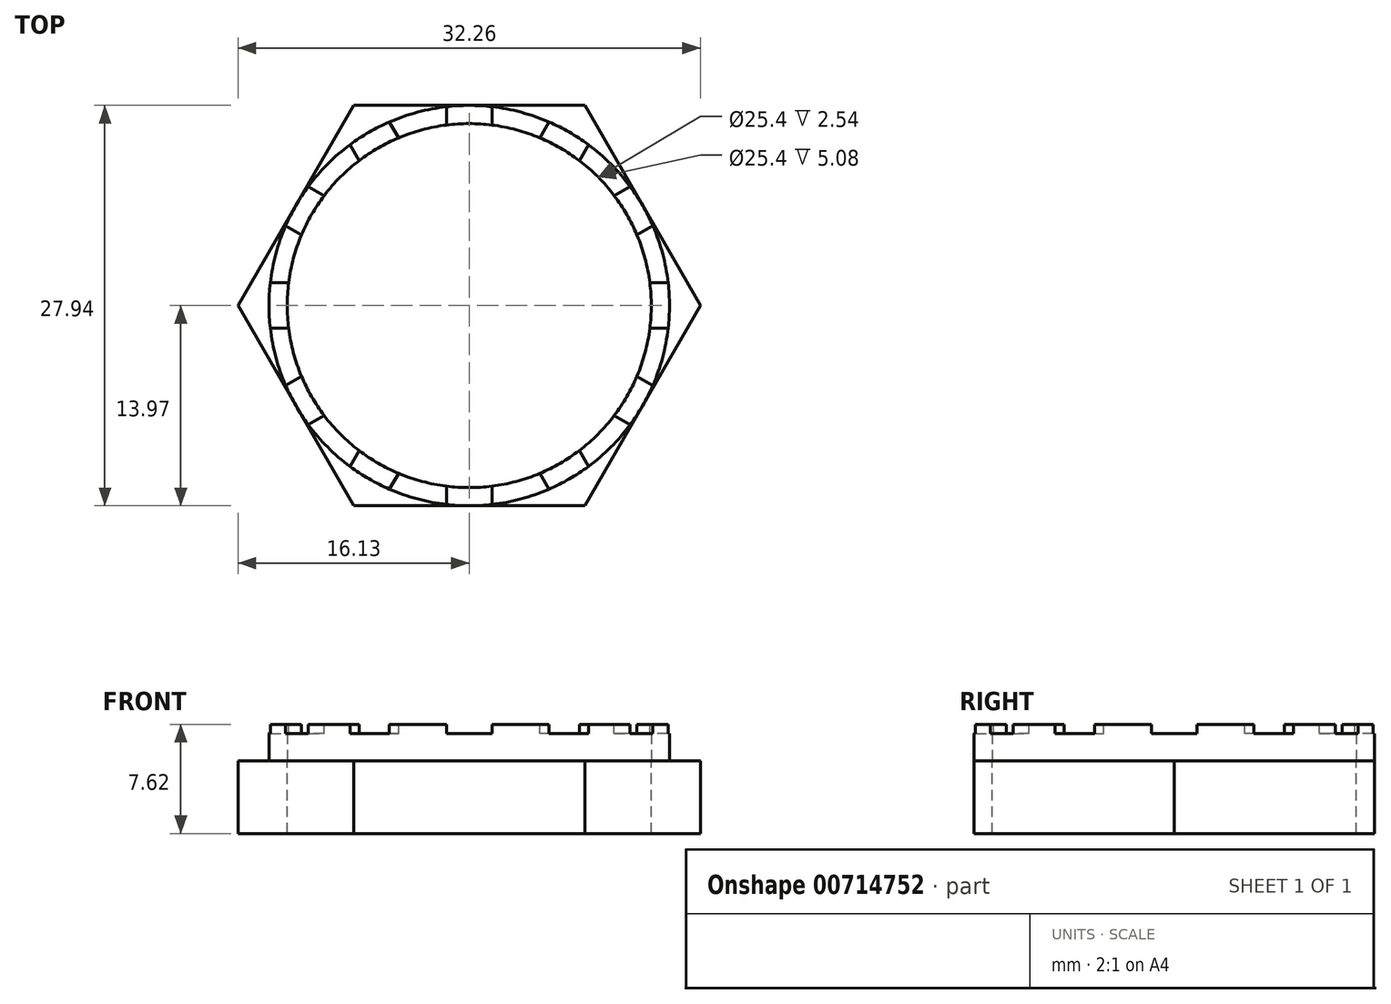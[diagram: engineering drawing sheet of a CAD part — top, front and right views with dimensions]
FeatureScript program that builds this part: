
annotation { "Feature Type Name" : "Feature", "Feature Type Description" : "" }
export const myFeature = defineFeature(function(context is Context, id is Id, definition is map)
    precondition{}
    {
        {
            var Q0;
            Q0=qCreatedBy(makeId("Top.planeOp"),FACE);
            var sketch = newSketch(context, id + "F0", { "sketchPlane" : qUnion([Q0])});
            skArc(sketch, "E0", {"start": v(1.59, 13.88) * mm, "mid": v(0, 13.97) * mm, "end": v(-1.59, 13.88) * mm});
            skArc(sketch, "E1", {"start": v(1.59, 12.6) * mm, "mid": v(0, 12.7) * mm, "end": v(-1.59, 12.6) * mm});
            skLineSegment(sketch, "E2", {"start": v(1.59, 13.88) * mm, "end": v(1.59, 12.6) * mm});
            skLineSegment(sketch, "E3", {"start": v(-1.59, 13.88) * mm, "end": v(-1.59, 12.6) * mm});
            skLineSegment(sketch, "E4.1.0", {"start": v(-8.31, 11.23) * mm, "end": v(-7.68, 10.12) * mm});
            skLineSegment(sketch, "E4.1.1", {"start": v(-5.56, 12.81) * mm, "end": v(-4.93, 11.7) * mm});
            skLineSegment(sketch, "E4.2.0", {"start": v(-12.81, 5.56) * mm, "end": v(-11.7, 4.93) * mm});
            skLineSegment(sketch, "E4.2.1", {"start": v(-11.23, 8.31) * mm, "end": v(-10.12, 7.68) * mm});
            skLineSegment(sketch, "E4.3.0", {"start": v(-13.88, -1.59) * mm, "end": v(-12.6, -1.59) * mm});
            skLineSegment(sketch, "E4.3.1", {"start": v(-13.88, 1.59) * mm, "end": v(-12.6, 1.59) * mm});
            skLineSegment(sketch, "E4.4.0", {"start": v(-11.23, -8.31) * mm, "end": v(-10.12, -7.68) * mm});
            skLineSegment(sketch, "E4.4.1", {"start": v(-12.81, -5.56) * mm, "end": v(-11.7, -4.93) * mm});
            skLineSegment(sketch, "E4.5.0", {"start": v(-5.56, -12.81) * mm, "end": v(-4.93, -11.7) * mm});
            skLineSegment(sketch, "E4.5.1", {"start": v(-8.31, -11.23) * mm, "end": v(-7.68, -10.12) * mm});
            skLineSegment(sketch, "E4.6.0", {"start": v(1.59, -13.88) * mm, "end": v(1.59, -12.6) * mm});
            skLineSegment(sketch, "E4.6.1", {"start": v(-1.59, -13.88) * mm, "end": v(-1.59, -12.6) * mm});
            skLineSegment(sketch, "E4.7.0", {"start": v(8.31, -11.23) * mm, "end": v(7.68, -10.12) * mm});
            skLineSegment(sketch, "E4.7.1", {"start": v(5.56, -12.81) * mm, "end": v(4.93, -11.7) * mm});
            skLineSegment(sketch, "E4.8.0", {"start": v(12.81, -5.56) * mm, "end": v(11.7, -4.93) * mm});
            skLineSegment(sketch, "E4.8.1", {"start": v(11.23, -8.31) * mm, "end": v(10.12, -7.68) * mm});
            skLineSegment(sketch, "E4.9.0", {"start": v(13.88, 1.59) * mm, "end": v(12.6, 1.59) * mm});
            skLineSegment(sketch, "E4.9.1", {"start": v(13.88, -1.59) * mm, "end": v(12.6, -1.59) * mm});
            skLineSegment(sketch, "E4.10.0", {"start": v(11.23, 8.31) * mm, "end": v(10.12, 7.68) * mm});
            skLineSegment(sketch, "E4.10.1", {"start": v(12.81, 5.56) * mm, "end": v(11.7, 4.93) * mm});
            skLineSegment(sketch, "E4.11.0", {"start": v(5.56, 12.81) * mm, "end": v(4.93, 11.7) * mm});
            skLineSegment(sketch, "E4.11.1", {"start": v(8.31, 11.23) * mm, "end": v(7.68, 10.12) * mm});
            skArc(sketch, "E5.trimOffspring", {"start": v(8.31, 11.23) * mm, "mid": v(6.99, 12.1) * mm, "end": v(5.56, 12.81) * mm});
            skArc(sketch, "E6.trimOffspring", {"start": v(7.68, 10.12) * mm, "mid": v(6.35, 11) * mm, "end": v(4.93, 11.7) * mm});
            skArc(sketch, "E7.trimOffspring", {"start": v(12.81, 5.56) * mm, "mid": v(12.1, 6.98) * mm, "end": v(11.23, 8.31) * mm});
            skArc(sketch, "E8.trimOffspring", {"start": v(11.7, 4.93) * mm, "mid": v(11, 6.35) * mm, "end": v(10.12, 7.68) * mm});
            skArc(sketch, "E9.trimOffspring", {"start": v(13.88, -1.59) * mm, "mid": v(13.97, 0) * mm, "end": v(13.88, 1.59) * mm});
            skArc(sketch, "E10.trimOffspring", {"start": v(12.6, -1.59) * mm, "mid": v(12.7, 0) * mm, "end": v(12.6, 1.59) * mm});
            skArc(sketch, "E11.trimOffspring", {"start": v(5.56, -12.81) * mm, "mid": v(6.98, -12.1) * mm, "end": v(8.31, -11.23) * mm});
            skArc(sketch, "E12.trimOffspring", {"start": v(4.93, -11.7) * mm, "mid": v(6.35, -11) * mm, "end": v(7.68, -10.12) * mm});
            skArc(sketch, "E13.trimOffspring", {"start": v(11.23, -8.31) * mm, "mid": v(12.1, -6.99) * mm, "end": v(12.81, -5.56) * mm});
            skArc(sketch, "E14.trimOffspring", {"start": v(10.12, -7.68) * mm, "mid": v(11, -6.35) * mm, "end": v(11.7, -4.93) * mm});
            skArc(sketch, "E15.trimOffspring", {"start": v(-1.59, -12.6) * mm, "mid": v(0, -12.7) * mm, "end": v(1.59, -12.6) * mm});
            skArc(sketch, "E16.trimOffspring", {"start": v(-1.59, -13.88) * mm, "mid": v(0, -13.97) * mm, "end": v(1.59, -13.88) * mm});
            skArc(sketch, "E17.trimOffspring", {"start": v(-8.31, -11.23) * mm, "mid": v(-6.99, -12.1) * mm, "end": v(-5.56, -12.81) * mm});
            skArc(sketch, "E18.trimOffspring", {"start": v(-7.68, -10.12) * mm, "mid": v(-6.35, -11) * mm, "end": v(-4.93, -11.7) * mm});
            skArc(sketch, "E19.trimOffspring", {"start": v(-11.7, -4.93) * mm, "mid": v(-11, -6.35) * mm, "end": v(-10.12, -7.68) * mm});
            skArc(sketch, "E20.trimOffspring", {"start": v(-12.81, -5.56) * mm, "mid": v(-12.1, -6.99) * mm, "end": v(-11.23, -8.31) * mm});
            skArc(sketch, "E21.trimOffspring", {"start": v(-12.6, 1.59) * mm, "mid": v(-12.7, 0) * mm, "end": v(-12.6, -1.59) * mm});
            skArc(sketch, "E22.trimOffspring", {"start": v(-13.88, 1.59) * mm, "mid": v(-13.97, 0) * mm, "end": v(-13.88, -1.59) * mm});
            skArc(sketch, "E23.trimOffspring", {"start": v(-11.23, 8.31) * mm, "mid": v(-12.1, 6.99) * mm, "end": v(-12.81, 5.56) * mm});
            skArc(sketch, "E24.trimOffspring", {"start": v(-10.12, 7.68) * mm, "mid": v(-11, 6.35) * mm, "end": v(-11.7, 4.93) * mm});
            skArc(sketch, "E25.trimOffspring", {"start": v(-4.93, 11.7) * mm, "mid": v(-6.35, 11) * mm, "end": v(-7.68, 10.12) * mm});
            skArc(sketch, "E26.trimOffspring", {"start": v(-5.56, 12.81) * mm, "mid": v(-6.98, 12.1) * mm, "end": v(-8.31, 11.23) * mm});
            skSolve(sketch);
        }
        {
            var Q0;
            Q0=qCreatedBy(makeId("Top.planeOp"),FACE);
            var sketch = newSketch(context, id + "F1", { "sketchPlane" : qUnion([Q0])});
            skCircle(sketch, "E27", {"center": v(0, 0) * mm, "radius": 13.97 * mm});
            skCircle(sketch, "E28", {"center": v(0, 0) * mm, "radius": 12.7 * mm});
            skLineSegment(sketch, "E29", {"start": v(-8.07, 13.97) * mm, "end": v(8.07, 13.97) * mm});
            skLineSegment(sketch, "E30", {"start": v(-8.07, -13.97) * mm, "end": v(8.07, -13.97) * mm});
            skPoint(sketch, "E31.orphan", {"position": v(0, 13.97) * mm});
            skPoint(sketch, "E32.orphan", {"position": v(0, -13.97) * mm});
            skLineSegment(sketch, "E33", {"start": v(8.07, 13.97) * mm, "end": v(16.13, 0) * mm});
            skLineSegment(sketch, "E34", {"start": v(8.07, -13.97) * mm, "end": v(16.13, 0) * mm});
            skLineSegment(sketch, "E35", {"start": v(-8.07, -13.97) * mm, "end": v(-16.13, 0) * mm});
            skLineSegment(sketch, "E36", {"start": v(-8.07, 13.97) * mm, "end": v(-16.13, 0) * mm});
            skSolve(sketch);
        }
        {
            var Q0;
            Q0=makeQuery(id+"F1.imprint","IMPRINT",FACE,{"disambiguationData":[TD([[makeQuery(id+"F1.imprint","IMPRINT",EDGE,{"derivedFrom":sQuery(id+"F1.wireOp",EDGE,"E28")}),-1.0]])]});
            extrude(context, id + "F2", {"entities" : qUnion([Q0]), "depth" : 2.54 * mm, "offsetDistance" : 25.4 * mm});
        }
        {
            var Q0;
            {var subQ0=sQuery(id+"F1.wireOp",EDGE,"E29");var subQ1=sQuery(id+"F1.wireOp",EDGE,"E27");var subQ2=makeQuery(id+"F1.imprint","INTERSECT",VERTEX,{"derivedFrom":[subQ1,subQ0]});Q0=makeQuery(id+"F1.imprint","IMPRINT",FACE,{"disambiguationData":[TD([[makeQuery(id+"F1.imprint","IMPRINT",EDGE,{"disambiguationData":[TD([[subQ2,-1.0]])],"derivedFrom":subQ1}),-1.0]])]});}
            var Q1;
            {var subQ0=sQuery(id+"F1.wireOp",EDGE,"E36");var subQ1=sQuery(id+"F1.wireOp",EDGE,"E27");var subQ2=makeQuery(id+"F1.imprint","INTERSECT",VERTEX,{"derivedFrom":[subQ1,subQ0]});Q1=makeQuery(id+"F1.imprint","IMPRINT",FACE,{"disambiguationData":[TD([[makeQuery(id+"F1.imprint","IMPRINT",EDGE,{"disambiguationData":[TD([[subQ2,-1.0]])],"derivedFrom":subQ1}),-1.0]])]});}
            var Q2;
            {var subQ0=sQuery(id+"F1.wireOp",EDGE,"E35");var subQ1=sQuery(id+"F1.wireOp",EDGE,"E27");var subQ2=makeQuery(id+"F1.imprint","INTERSECT",VERTEX,{"derivedFrom":[subQ1,subQ0]});Q2=makeQuery(id+"F1.imprint","IMPRINT",FACE,{"disambiguationData":[TD([[makeQuery(id+"F1.imprint","IMPRINT",EDGE,{"disambiguationData":[TD([[subQ2,-1.0]])],"derivedFrom":subQ1}),-1.0]])]});}
            var Q3;
            {var subQ0=sQuery(id+"F1.wireOp",EDGE,"E30");var subQ1=sQuery(id+"F1.wireOp",EDGE,"E27");var subQ2=makeQuery(id+"F1.imprint","INTERSECT",VERTEX,{"derivedFrom":[subQ1,subQ0]});Q3=makeQuery(id+"F1.imprint","IMPRINT",FACE,{"disambiguationData":[TD([[makeQuery(id+"F1.imprint","IMPRINT",EDGE,{"disambiguationData":[TD([[subQ2,-1.0]])],"derivedFrom":subQ1}),-1.0]])]});}
            var Q4;
            {var subQ0=sQuery(id+"F1.wireOp",EDGE,"E33");var subQ1=sQuery(id+"F1.wireOp",EDGE,"E27");var subQ2=makeQuery(id+"F1.imprint","INTERSECT",VERTEX,{"derivedFrom":[subQ1,subQ0]});Q4=makeQuery(id+"F1.imprint","IMPRINT",FACE,{"disambiguationData":[TD([[makeQuery(id+"F1.imprint","IMPRINT",EDGE,{"disambiguationData":[TD([[subQ2,1.0]])],"derivedFrom":subQ1}),-1.0]])]});}
            var Q5;
            {var subQ0=sQuery(id+"F1.wireOp",EDGE,"E29");var subQ1=sQuery(id+"F1.wireOp",EDGE,"E27");var subQ2=makeQuery(id+"F1.imprint","INTERSECT",VERTEX,{"derivedFrom":[subQ1,subQ0]});Q5=makeQuery(id+"F1.imprint","IMPRINT",FACE,{"disambiguationData":[TD([[makeQuery(id+"F1.imprint","IMPRINT",EDGE,{"disambiguationData":[TD([[subQ2,1.0]])],"derivedFrom":subQ1}),-1.0]])]});}
            var Q6;
            Q6=makeQuery(id+"F1.imprint","IMPRINT",FACE,{"disambiguationData":[TD([[makeQuery(id+"F1.imprint","IMPRINT",EDGE,{"derivedFrom":sQuery(id+"F1.wireOp",EDGE,"E28")}),-1.0]])]});
            extrude(context, id + "F3", {"entities" : qUnion([Q0, Q1, Q2, Q3, Q4, Q5, Q6]), "oppositeDirection" : true, "depth" : 5.08 * mm, "offsetDistance" : 25.4 * mm});
        }
        {
            var Q0;
            Q0=makeQuery(id+"F2.opExtrude","CAP_FACE",FACE,{"disambiguationData":[OSD([sQuery(id+"F1.wireOp",EDGE,"E27"),sQuery(id+"F1.wireOp",EDGE,"E28")])],"isStart":false});
            var sketch = newSketch(context, id + "F4", { "sketchPlane" : qUnion([Q0])});
            skLineSegment(sketch, "E37.0", {"start": v(-8.31, 11.23) * mm, "end": v(-7.68, 10.12) * mm});
            skArc(sketch, "E38.0", {"start": v(-5.56, 12.81) * mm, "mid": v(-6.98, 12.1) * mm, "end": v(-8.31, 11.23) * mm});
            skLineSegment(sketch, "E39.0", {"start": v(-5.56, 12.81) * mm, "end": v(-4.93, 11.7) * mm});
            skArc(sketch, "E40.0", {"start": v(-4.93, 11.7) * mm, "mid": v(-6.35, 11) * mm, "end": v(-7.68, 10.12) * mm});
            skArc(sketch, "E41.0", {"start": v(1.59, 13.88) * mm, "mid": v(0, 13.97) * mm, "end": v(-1.59, 13.88) * mm});
            skLineSegment(sketch, "E42.0", {"start": v(-1.59, 13.88) * mm, "end": v(-1.59, 12.6) * mm});
            skArc(sketch, "E43.0", {"start": v(1.59, 12.6) * mm, "mid": v(0, 12.7) * mm, "end": v(-1.59, 12.6) * mm});
            skLineSegment(sketch, "E44.0", {"start": v(1.59, 13.88) * mm, "end": v(1.59, 12.6) * mm});
            skLineSegment(sketch, "E45.0", {"start": v(-11.23, 8.31) * mm, "end": v(-10.12, 7.68) * mm});
            skArc(sketch, "E46.0", {"start": v(-11.23, 8.31) * mm, "mid": v(-12.1, 6.99) * mm, "end": v(-12.81, 5.56) * mm});
            skArc(sketch, "E47.0", {"start": v(-10.12, 7.68) * mm, "mid": v(-11, 6.35) * mm, "end": v(-11.7, 4.93) * mm});
            skLineSegment(sketch, "E48.0", {"start": v(-12.81, 5.56) * mm, "end": v(-11.7, 4.93) * mm});
            skLineSegment(sketch, "E49.0", {"start": v(-13.88, 1.59) * mm, "end": v(-12.6, 1.59) * mm});
            skArc(sketch, "E50.0", {"start": v(-12.6, 1.59) * mm, "mid": v(-12.7, 0) * mm, "end": v(-12.6, -1.59) * mm});
            skArc(sketch, "E51.0", {"start": v(-13.88, 1.59) * mm, "mid": v(-13.97, 0) * mm, "end": v(-13.88, -1.59) * mm});
            skLineSegment(sketch, "E52.0", {"start": v(-13.88, -1.59) * mm, "end": v(-12.6, -1.59) * mm});
            skLineSegment(sketch, "E53.0", {"start": v(-12.81, -5.56) * mm, "end": v(-11.7, -4.93) * mm});
            skArc(sketch, "E54.0", {"start": v(-11.7, -4.93) * mm, "mid": v(-11, -6.35) * mm, "end": v(-10.12, -7.68) * mm});
            skLineSegment(sketch, "E55.0", {"start": v(-11.23, -8.31) * mm, "end": v(-10.12, -7.68) * mm});
            skArc(sketch, "E56.0", {"start": v(-12.81, -5.56) * mm, "mid": v(-12.1, -6.99) * mm, "end": v(-11.23, -8.31) * mm});
            skArc(sketch, "E57.0", {"start": v(-7.68, -10.12) * mm, "mid": v(-6.35, -11) * mm, "end": v(-4.93, -11.7) * mm});
            skLineSegment(sketch, "E58.0", {"start": v(-8.31, -11.23) * mm, "end": v(-7.68, -10.12) * mm});
            skLineSegment(sketch, "E59.0", {"start": v(-5.56, -12.81) * mm, "end": v(-4.93, -11.7) * mm});
            skArc(sketch, "E60.0", {"start": v(-8.31, -11.23) * mm, "mid": v(-6.99, -12.1) * mm, "end": v(-5.56, -12.81) * mm});
            skArc(sketch, "E61.0", {"start": v(-1.59, -12.6) * mm, "mid": v(0, -12.7) * mm, "end": v(1.59, -12.6) * mm});
            skLineSegment(sketch, "E62.0", {"start": v(1.59, -13.88) * mm, "end": v(1.59, -12.6) * mm});
            skLineSegment(sketch, "E63.0", {"start": v(-1.59, -13.88) * mm, "end": v(-1.59, -12.6) * mm});
            skArc(sketch, "E64.0", {"start": v(-1.59, -13.88) * mm, "mid": v(0, -13.97) * mm, "end": v(1.59, -13.88) * mm});
            skLineSegment(sketch, "E65.0", {"start": v(5.56, -12.81) * mm, "end": v(4.93, -11.7) * mm});
            skArc(sketch, "E66.0", {"start": v(4.93, -11.7) * mm, "mid": v(6.35, -11) * mm, "end": v(7.68, -10.12) * mm});
            skArc(sketch, "E67.0", {"start": v(5.56, -12.81) * mm, "mid": v(6.98, -12.1) * mm, "end": v(8.31, -11.23) * mm});
            skLineSegment(sketch, "E68.0", {"start": v(8.31, -11.23) * mm, "end": v(7.68, -10.12) * mm});
            skLineSegment(sketch, "E69.0", {"start": v(11.23, -8.31) * mm, "end": v(10.12, -7.68) * mm});
            skArc(sketch, "E70.0", {"start": v(11.23, -8.31) * mm, "mid": v(12.1, -6.99) * mm, "end": v(12.81, -5.56) * mm});
            skArc(sketch, "E71.0", {"start": v(10.12, -7.68) * mm, "mid": v(11, -6.35) * mm, "end": v(11.7, -4.93) * mm});
            skLineSegment(sketch, "E72.0", {"start": v(12.81, -5.56) * mm, "end": v(11.7, -4.93) * mm});
            skLineSegment(sketch, "E73.0", {"start": v(13.88, -1.59) * mm, "end": v(12.6, -1.59) * mm});
            skArc(sketch, "E74.0", {"start": v(12.6, -1.59) * mm, "mid": v(12.7, 0) * mm, "end": v(12.6, 1.59) * mm});
            skLineSegment(sketch, "E75.0", {"start": v(13.88, 1.59) * mm, "end": v(12.6, 1.59) * mm});
            skArc(sketch, "E76.0", {"start": v(13.88, -1.59) * mm, "mid": v(13.97, 0) * mm, "end": v(13.88, 1.59) * mm});
            skArc(sketch, "E77.0", {"start": v(11.7, 4.93) * mm, "mid": v(11, 6.35) * mm, "end": v(10.12, 7.68) * mm});
            skLineSegment(sketch, "E78.0", {"start": v(11.23, 8.31) * mm, "end": v(10.12, 7.68) * mm});
            skArc(sketch, "E79.0", {"start": v(12.81, 5.56) * mm, "mid": v(12.1, 6.98) * mm, "end": v(11.23, 8.31) * mm});
            skLineSegment(sketch, "E80.0", {"start": v(12.81, 5.56) * mm, "end": v(11.7, 4.93) * mm});
            skLineSegment(sketch, "E81.0", {"start": v(8.31, 11.23) * mm, "end": v(7.68, 10.12) * mm});
            skArc(sketch, "E82.0", {"start": v(8.31, 11.23) * mm, "mid": v(6.99, 12.1) * mm, "end": v(5.56, 12.81) * mm});
            skLineSegment(sketch, "E83.0", {"start": v(5.56, 12.81) * mm, "end": v(4.93, 11.7) * mm});
            skArc(sketch, "E84.0", {"start": v(7.68, 10.12) * mm, "mid": v(6.35, 11) * mm, "end": v(4.93, 11.7) * mm});
            skSolve(sketch);
        }
        {
            var Q0;
            Q0=makeQuery(id+"F4.imprint","IMPRINT",FACE,{"disambiguationData":[TD([[makeQuery(id+"F4.imprint","IMPRINT",EDGE,{"derivedFrom":sQuery(id+"F4.wireOp",EDGE,"E49.0")}),-1.0]])]});
            var Q1;
            Q1=makeQuery(id+"F4.imprint","IMPRINT",FACE,{"disambiguationData":[TD([[makeQuery(id+"F4.imprint","IMPRINT",EDGE,{"derivedFrom":sQuery(id+"F4.wireOp",EDGE,"E45.0")}),-1.0]])]});
            var Q2;
            Q2=makeQuery(id+"F4.imprint","IMPRINT",FACE,{"disambiguationData":[TD([[makeQuery(id+"F4.imprint","IMPRINT",EDGE,{"derivedFrom":sQuery(id+"F4.wireOp",EDGE,"E37.0")}),1.0]])]});
            var Q3;
            Q3=makeQuery(id+"F4.imprint","IMPRINT",FACE,{"disambiguationData":[TD([[makeQuery(id+"F4.imprint","IMPRINT",EDGE,{"derivedFrom":sQuery(id+"F4.wireOp",EDGE,"E41.0")}),1.0]])]});
            var Q4;
            Q4=makeQuery(id+"F4.imprint","IMPRINT",FACE,{"disambiguationData":[TD([[makeQuery(id+"F4.imprint","IMPRINT",EDGE,{"derivedFrom":sQuery(id+"F4.wireOp",EDGE,"E81.0")}),-1.0]])]});
            var Q5;
            Q5=makeQuery(id+"F4.imprint","IMPRINT",FACE,{"disambiguationData":[TD([[makeQuery(id+"F4.imprint","IMPRINT",EDGE,{"derivedFrom":sQuery(id+"F4.wireOp",EDGE,"E73.0")}),-1.0]])]});
            var Q6;
            Q6=makeQuery(id+"F4.imprint","IMPRINT",FACE,{"disambiguationData":[TD([[makeQuery(id+"F4.imprint","IMPRINT",EDGE,{"derivedFrom":sQuery(id+"F4.wireOp",EDGE,"E69.0")}),-1.0]])]});
            var Q7;
            Q7=makeQuery(id+"F4.imprint","IMPRINT",FACE,{"disambiguationData":[TD([[makeQuery(id+"F4.imprint","IMPRINT",EDGE,{"derivedFrom":sQuery(id+"F4.wireOp",EDGE,"E65.0")}),-1.0]])]});
            var Q8;
            Q8=makeQuery(id+"F4.imprint","IMPRINT",FACE,{"disambiguationData":[TD([[makeQuery(id+"F4.imprint","IMPRINT",EDGE,{"derivedFrom":sQuery(id+"F4.wireOp",EDGE,"E61.0")}),-1.0]])]});
            var Q9;
            Q9=makeQuery(id+"F4.imprint","IMPRINT",FACE,{"disambiguationData":[TD([[makeQuery(id+"F4.imprint","IMPRINT",EDGE,{"derivedFrom":sQuery(id+"F4.wireOp",EDGE,"E57.0")}),-1.0]])]});
            var Q10;
            Q10=makeQuery(id+"F4.imprint","IMPRINT",FACE,{"disambiguationData":[TD([[makeQuery(id+"F4.imprint","IMPRINT",EDGE,{"derivedFrom":sQuery(id+"F4.wireOp",EDGE,"E53.0")}),-1.0]])]});
            var Q11;
            Q11=makeQuery(id+"F4.imprint","IMPRINT",FACE,{"disambiguationData":[TD([[makeQuery(id+"F4.imprint","IMPRINT",EDGE,{"derivedFrom":sQuery(id+"F4.wireOp",EDGE,"E77.0")}),-1.0]])]});
            extrude(context, id + "F5", {"entities" : qUnion([Q0, Q1, Q2, Q3, Q4, Q5, Q6, Q7, Q8, Q9, Q10, Q11]), "operationType" : NewBodyOperationType.REMOVE, "oppositeDirection" : true, "depth" : 0.64 * mm, "offsetDistance" : 25.4 * mm});
        }
    });
